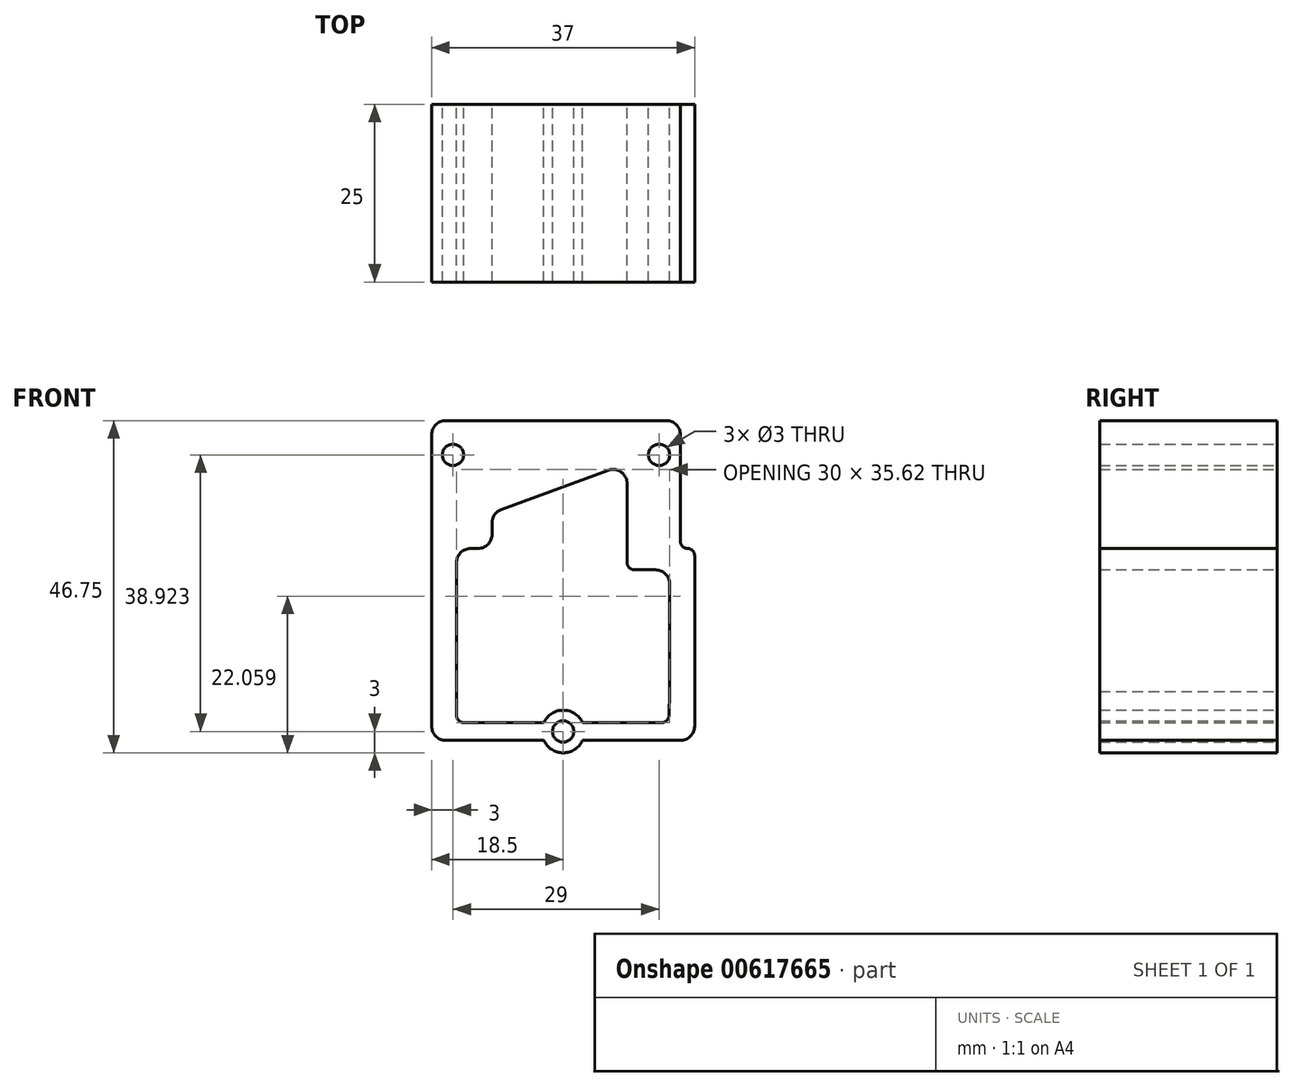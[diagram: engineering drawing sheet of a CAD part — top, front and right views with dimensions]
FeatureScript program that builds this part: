
annotation { "Feature Type Name" : "Feature", "Feature Type Description" : "" }
export const myFeature = defineFeature(function(context is Context, id is Id, definition is map)
    precondition{}
    {
        {
            var Q0;
            Q0=qCreatedBy(makeId("Front.planeOp"),FACE);
            var sketch = newSketch(context, id + "F0", { "sketchPlane" : qUnion([Q0])});
            skLineSegment(sketch, "E0.bottom", {"start": v(-16.5, 22.5) * mm, "end": v(14.5, 22.5) * mm});
            skLineSegment(sketch, "E0.top", {"start": v(-16.5, -22.5) * mm, "end": v(16.5, -22.5) * mm});
            skLineSegment(sketch, "E0.left", {"start": v(-18.5, 20.5) * mm, "end": v(-18.5, -20.5) * mm});
            skLineSegment(sketch, "E0.right", {"start": v(18.5, 3.5) * mm, "end": v(18.5, -20.5) * mm});
            skPoint(sketch, "E0.middle", {"position": v(0, 0) * mm});
            skLineSegment(sketch, "E1", {"start": v(-15, 2.5) * mm, "end": v(-15, -15.5) * mm});
            skLineSegment(sketch, "E2", {"start": v(-13, -17.5) * mm, "end": v(13, -17.5) * mm});
            skLineSegment(sketch, "E3", {"start": v(15, -15.5) * mm, "end": v(15, -0.5) * mm});
            skLineSegment(sketch, "E4", {"start": v(-13, 4.5) * mm, "end": v(-12, 4.5) * mm});
            skLineSegment(sketch, "E5", {"start": v(-10, 6.5) * mm, "end": v(-10, 8.1) * mm});
            skLineSegment(sketch, "E6", {"start": v(-8.7, 9.98) * mm, "end": v(6.3, 15.5) * mm});
            skLineSegment(sketch, "E7", {"start": v(9, 13.63) * mm, "end": v(9, 2.5) * mm});
            skLineSegment(sketch, "E8", {"start": v(10, 1.5) * mm, "end": v(13, 1.5) * mm});
            skLineSegment(sketch, "E9", {"start": v(16.5, 20.5) * mm, "end": v(16.5, 5.5) * mm});
            skLineSegment(sketch, "E10", {"start": v(17.5, 4.5) * mm, "end": v(17.5, 4.5) * mm});
            skPoint(sketch, "E11.visualSharp", {"position": v(-15, 4.5) * mm});
            skArc(sketch, "E11.filletArc", {"start": v(-13, 4.5) * mm, "mid": v(-14.41, 3.91) * mm, "end": v(-15, 2.5) * mm});
            skPoint(sketch, "E12.visualSharp", {"position": v(-10, 4.5) * mm});
            skArc(sketch, "E12.filletArc", {"start": v(-12, 4.5) * mm, "mid": v(-10.59, 5.09) * mm, "end": v(-10, 6.5) * mm});
            skPoint(sketch, "E13.visualSharp", {"position": v(-10, 9.5) * mm});
            skArc(sketch, "E13.filletArc", {"start": v(-8.7, 9.98) * mm, "mid": v(-9.64, 9.25) * mm, "end": v(-10, 8.1) * mm});
            skPoint(sketch, "E14.visualSharp", {"position": v(9, 16.5) * mm});
            skArc(sketch, "E14.filletArc", {"start": v(9, 13.63) * mm, "mid": v(8.14, 15.27) * mm, "end": v(6.3, 15.5) * mm});
            skPoint(sketch, "E15.visualSharp", {"position": v(9, 1.5) * mm});
            skArc(sketch, "E15.filletArc", {"start": v(9, 2.5) * mm, "mid": v(9.3, 1.8) * mm, "end": v(10, 1.5) * mm});
            skPoint(sketch, "E16.visualSharp", {"position": v(15, 1.5) * mm});
            skArc(sketch, "E16.filletArc", {"start": v(15, -0.5) * mm, "mid": v(14.41, 0.91) * mm, "end": v(13, 1.5) * mm});
            skPoint(sketch, "E17.visualSharp", {"position": v(-15, -17.5) * mm});
            skArc(sketch, "E17.filletArc", {"start": v(-15, -15.5) * mm, "mid": v(-14.41, -16.91) * mm, "end": v(-13, -17.5) * mm});
            skPoint(sketch, "E18.visualSharp", {"position": v(15, -17.5) * mm});
            skArc(sketch, "E18.filletArc", {"start": v(13, -17.5) * mm, "mid": v(14.41, -16.91) * mm, "end": v(15, -15.5) * mm});
            skLineSegment(sketch, "E19", {"start": v(-14, -20) * mm, "end": v(13.89, -20) * mm});
            skLineSegment(sketch, "E20", {"start": v(-15, -15.5) * mm, "end": v(-15, -19) * mm});
            skLineSegment(sketch, "E21", {"start": v(15, -15.5) * mm, "end": v(14.89, -19.03) * mm});
            skPoint(sketch, "E22.visualSharp", {"position": v(-15, -20) * mm});
            skArc(sketch, "E22.filletArc", {"start": v(-15, -19) * mm, "mid": v(-14.7, -19.7) * mm, "end": v(-14, -20) * mm});
            skPoint(sketch, "E23.visualSharp", {"position": v(14.86, -20) * mm});
            skArc(sketch, "E23.filletArc", {"start": v(13.89, -20) * mm, "mid": v(14.58, -19.72) * mm, "end": v(14.89, -19.03) * mm});
            skLineSegment(sketch, "E24", {"start": v(0, -17.5) * mm, "end": v(0, -22.5) * mm, "construction": true});
            skCircle(sketch, "E25", {"center": v(0, -21.25) * mm, "radius": 3 * mm});
            skCircle(sketch, "E26", {"center": v(0, -21.25) * mm, "radius": 1.5 * mm});
            skPoint(sketch, "E27.visualSharp", {"position": v(-18.5, 22.5) * mm});
            skArc(sketch, "E27.filletArc", {"start": v(-16.5, 22.5) * mm, "mid": v(-17.91, 21.91) * mm, "end": v(-18.5, 20.5) * mm});
            skPoint(sketch, "E28.visualSharp", {"position": v(16.5, 22.5) * mm});
            skArc(sketch, "E28.filletArc", {"start": v(16.5, 20.5) * mm, "mid": v(15.91, 21.91) * mm, "end": v(14.5, 22.5) * mm});
            skPoint(sketch, "E29.visualSharp", {"position": v(16.5, 4.5) * mm});
            skArc(sketch, "E29.filletArc", {"start": v(16.5, 5.5) * mm, "mid": v(16.8, 4.8) * mm, "end": v(17.5, 4.5) * mm});
            skPoint(sketch, "E30.visualSharp", {"position": v(18.5, 4.5) * mm});
            skArc(sketch, "E30.filletArc", {"start": v(18.5, 3.5) * mm, "mid": v(18.2, 4.2) * mm, "end": v(17.5, 4.5) * mm});
            skCircle(sketch, "E31", {"center": v(-15.5, 17.67) * mm, "radius": 3 * mm});
            skCircle(sketch, "E32", {"center": v(-15.5, 17.67) * mm, "radius": 1.5 * mm});
            skLineSegment(sketch, "E33", {"start": v(-15.5, 17.67) * mm, "end": v(13.5, 17.67) * mm, "construction": true});
            skCircle(sketch, "E34", {"center": v(13.5, 17.67) * mm, "radius": 3 * mm});
            skCircle(sketch, "E35", {"center": v(13.5, 17.67) * mm, "radius": 1.5 * mm});
            skPoint(sketch, "E36.visualSharp", {"position": v(-18.5, -22.5) * mm});
            skArc(sketch, "E36.filletArc", {"start": v(-18.5, -20.5) * mm, "mid": v(-17.91, -21.91) * mm, "end": v(-16.5, -22.5) * mm});
            skPoint(sketch, "E37.visualSharp", {"position": v(18.5, -22.5) * mm});
            skArc(sketch, "E37.filletArc", {"start": v(16.5, -22.5) * mm, "mid": v(17.91, -21.91) * mm, "end": v(18.5, -20.5) * mm});
            skSolve(sketch);
        }
        {
            var Q0;
            Q0=makeQuery(id+"F0.imprint","IMPRINT",FACE,{"disambiguationData":[TD([[makeQuery(id+"F0.imprint","IMPRINT",EDGE,{"derivedFrom":sQuery(id+"F0.wireOp",EDGE,"E0.bottom")}),-1.0]])]});
            var Q1;
            {var subQ0=sQuery(id+"F0.wireOp",EDGE,"E25");var subQ1=sQuery(id+"F0.wireOp",EDGE,"E0.top");var subQ2=makeQuery(id+"F0.imprint","INTERSECT",VERTEX,{"disambiguationData":[OD(0.0)],"derivedFrom":[subQ1,subQ0]});Q1=makeQuery(id+"F0.imprint","IMPRINT",FACE,{"disambiguationData":[TD([[makeQuery(id+"F0.imprint","IMPRINT",EDGE,{"disambiguationData":[TD([[subQ2,-1.0]])],"derivedFrom":subQ1}),1.0]])]});}
            var Q2;
            {var subQ0=sQuery(id+"F0.wireOp",EDGE,"E25");var subQ1=sQuery(id+"F0.wireOp",EDGE,"E0.top");var subQ2=makeQuery(id+"F0.imprint","INTERSECT",VERTEX,{"disambiguationData":[OD(0.0)],"derivedFrom":[subQ1,subQ0]});Q2=makeQuery(id+"F0.imprint","IMPRINT",FACE,{"disambiguationData":[TD([[makeQuery(id+"F0.imprint","IMPRINT",EDGE,{"disambiguationData":[TD([[subQ2,-1.0]])],"derivedFrom":subQ1}),1.0]])]});}
            var Q3;
            {var subQ0=sQuery(id+"F0.wireOp",EDGE,"E25");var subQ1=sQuery(id+"F0.wireOp",EDGE,"E0.top");var subQ2=makeQuery(id+"F0.imprint","INTERSECT",VERTEX,{"disambiguationData":[OD(0.0)],"derivedFrom":[subQ1,subQ0]});Q3=makeQuery(id+"F0.imprint","IMPRINT",FACE,{"disambiguationData":[TD([[makeQuery(id+"F0.imprint","IMPRINT",EDGE,{"disambiguationData":[TD([[subQ2,-1.0]])],"derivedFrom":subQ1}),-1.0]])]});}
            var Q4;
            {var subQ0=sQuery(id+"F0.wireOp",EDGE,"E25");var subQ1=sQuery(id+"F0.wireOp",EDGE,"E0.top");var subQ2=makeQuery(id+"F0.imprint","INTERSECT",VERTEX,{"disambiguationData":[OD(1.0)],"derivedFrom":[subQ1,subQ0]});Q4=makeQuery(id+"F0.imprint","IMPRINT",FACE,{"disambiguationData":[TD([[makeQuery(id+"F0.imprint","IMPRINT",EDGE,{"disambiguationData":[TD([[subQ2,1.0]])],"derivedFrom":subQ1}),1.0]])]});}
            var Q5;
            {var subQ0=sQuery(id+"F0.wireOp",EDGE,"E25");var subQ1=sQuery(id+"F0.wireOp",EDGE,"E19");var subQ2=makeQuery(id+"F0.imprint","INTERSECT",VERTEX,{"disambiguationData":[OD(0.0)],"derivedFrom":[subQ1,subQ0]});Q5=makeQuery(id+"F0.imprint","IMPRINT",FACE,{"disambiguationData":[TD([[makeQuery(id+"F0.imprint","IMPRINT",EDGE,{"disambiguationData":[TD([[subQ2,-1.0]])],"derivedFrom":subQ1}),1.0]])]});}
            var Q6;
            Q6=makeQuery(id+"F0.imprint","IMPRINT",FACE,{"disambiguationData":[TD([[makeQuery(id+"F0.imprint","IMPRINT",EDGE,{"derivedFrom":sQuery(id+"F0.wireOp",EDGE,"E31")}),1.0]])]});
            var Q7;
            Q7=makeQuery(id+"F0.imprint","IMPRINT",FACE,{"disambiguationData":[TD([[makeQuery(id+"F0.imprint","IMPRINT",EDGE,{"derivedFrom":sQuery(id+"F0.wireOp",EDGE,"E34")}),1.0]])]});
            extrude(context, id + "F1", {"entities" : qUnion([Q0, Q1, Q2, Q3, Q4, Q5, Q6, Q7]), "depth" : 25 * mm, "offsetDistance" : 25 * mm});
        }
    });
